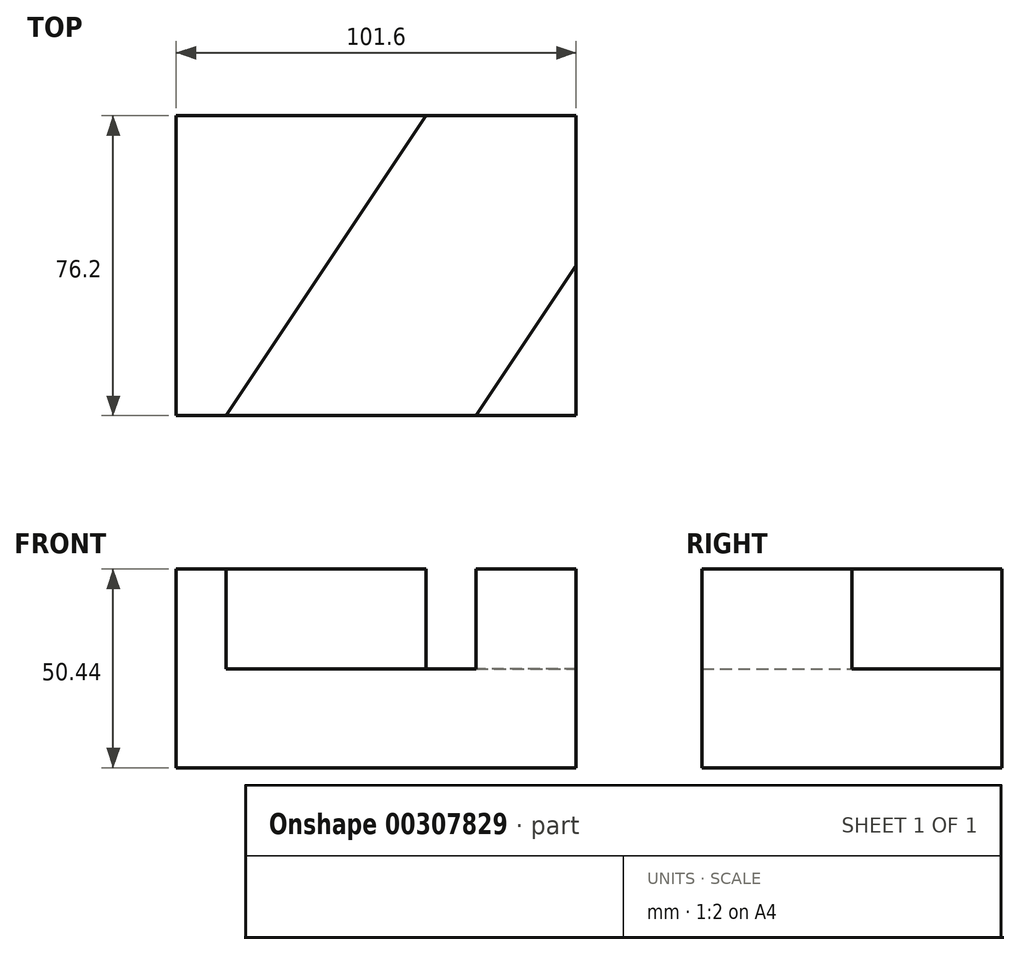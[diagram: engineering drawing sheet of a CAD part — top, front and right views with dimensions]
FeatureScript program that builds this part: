
annotation { "Feature Type Name" : "Feature", "Feature Type Description" : "" }
export const myFeature = defineFeature(function(context is Context, id is Id, definition is map)
    precondition{}
    {
        {
            var Q0;
            Q0=qCreatedBy(makeId("Front.planeOp"),FACE);
            var sketch = newSketch(context, id + "F0", { "sketchPlane" : qUnion([Q0])});
            skLineSegment(sketch, "E0", {"start": v(-49.12, -55.67) * mm, "end": v(52.48, -55.67) * mm});
            skLineSegment(sketch, "E1", {"start": v(52.48, -55.67) * mm, "end": v(52.48, -30.63) * mm});
            skLineSegment(sketch, "E2", {"start": v(52.48, -30.63) * mm, "end": v(-49.12, -30.63) * mm});
            skLineSegment(sketch, "E3", {"start": v(-49.12, -30.63) * mm, "end": v(-49.12, -55.67) * mm});
            skSolve(sketch);
        }
        {
            var Q0;
            Q0=makeQuery(id+"F0.imprint","IMPRINT",FACE,{"disambiguationData":[TD([[makeQuery(id+"F0.imprint","IMPRINT",EDGE,{"derivedFrom":sQuery(id+"F0.wireOp",EDGE,"E0")}),1.0]])]});
            extrude(context, id + "F1", {"entities" : qUnion([Q0]), "depth" : 76.2 * mm});
        }
        {
            var Q0;
            Q0=makeQuery(id+"F1.opExtrude","SWEPT_FACE",FACE,{"disambiguationData":[OSD([sQuery(id+"F0.wireOp",EDGE,"E2")])]});
            var sketch = newSketch(context, id + "F2", { "sketchPlane" : qUnion([Q0])});
            skLineSegment(sketch, "E4", {"start": v(-36.42, -76.2) * mm, "end": v(-49.12, -76.2) * mm});
            skLineSegment(sketch, "E5", {"start": v(-49.12, -76.2) * mm, "end": v(-49.12, 0) * mm});
            skLineSegment(sketch, "E6", {"start": v(-49.12, 0) * mm, "end": v(14.38, 0) * mm});
            skLineSegment(sketch, "E7", {"start": v(-36.42, -76.2) * mm, "end": v(14.38, 0) * mm});
            skSolve(sketch);
        }
        {
            var Q0;
            Q0=makeQuery(id+"F2.imprint","IMPRINT",FACE,{"disambiguationData":[TD([[makeQuery(id+"F2.imprint","IMPRINT",EDGE,{"derivedFrom":sQuery(id+"F2.wireOp",EDGE,"E4")}),-1.0]])]});
            extrude(context, id + "F3", {"entities" : qUnion([Q0]), "operationType" : NewBodyOperationType.ADD, "depth" : 25.4 * mm});
        }
        {
            var Q0;
            Q0=makeQuery(id+"F1.opExtrude","SWEPT_FACE",FACE,{"disambiguationData":[OSD([sQuery(id+"F0.wireOp",EDGE,"E2")])]});
            var sketch = newSketch(context, id + "F4", { "sketchPlane" : qUnion([Q0])});
            skLineSegment(sketch, "E8", {"start": v(52.48, -76.2) * mm, "end": v(52.48, -38.1) * mm});
            skLineSegment(sketch, "E9", {"start": v(52.48, -76.2) * mm, "end": v(27.08, -76.2) * mm});
            skLineSegment(sketch, "E10", {"start": v(27.08, -76.2) * mm, "end": v(52.48, -38.1) * mm});
            skSolve(sketch);
        }
        {
            var Q0;
            Q0=makeQuery(id+"F4.imprint","IMPRINT",FACE,{"disambiguationData":[TD([[makeQuery(id+"F4.imprint","IMPRINT",EDGE,{"derivedFrom":sQuery(id+"F4.wireOp",EDGE,"E8")}),1.0]])]});
            extrude(context, id + "F5", {"entities" : qUnion([Q0]), "operationType" : NewBodyOperationType.ADD, "depth" : 25.4 * mm});
        }
    });
